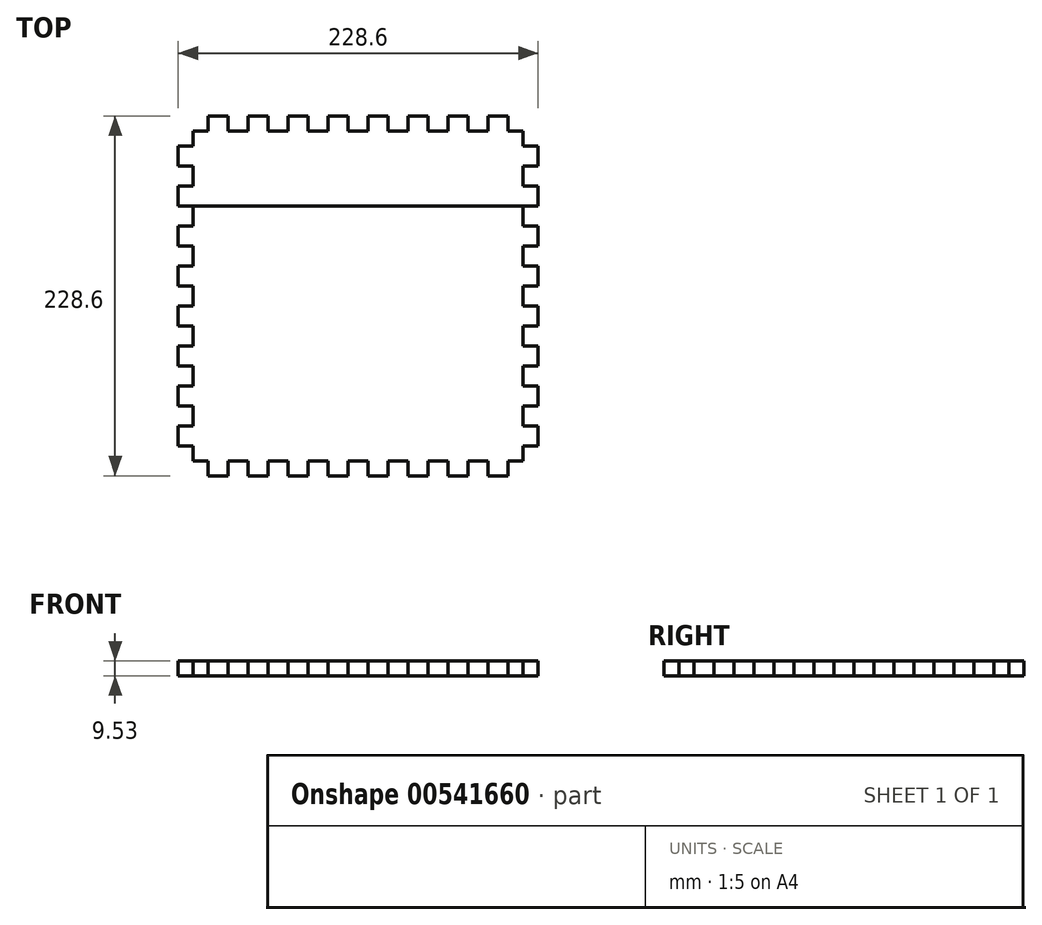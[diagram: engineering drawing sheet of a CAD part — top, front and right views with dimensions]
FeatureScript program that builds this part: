
annotation { "Feature Type Name" : "Feature", "Feature Type Description" : "" }
export const myFeature = defineFeature(function(context is Context, id is Id, definition is map)
    precondition{}
    {
        {
            var Q0;
            Q0=qCreatedBy(makeId("Top.planeOp"),FACE);
            var sketch = newSketch(context, id + "F0", { "sketchPlane" : qUnion([Q0])});
            skLineSegment(sketch, "E0.bottom", {"start": v(19.05, 0) * mm, "end": v(31.75, 0) * mm});
            skLineSegment(sketch, "E0.left", {"start": v(0, 0) * mm, "end": v(0, -31.75) * mm});
            skLineSegment(sketch, "E1", {"start": v(9.52, -9.52) * mm, "end": v(19.05, -9.52) * mm});
            skLineSegment(sketch, "E2", {"start": v(19.05, -9.53) * mm, "end": v(19.05, 0) * mm});
            skLineSegment(sketch, "E3", {"start": v(31.75, 0) * mm, "end": v(31.75, -9.53) * mm});
            skLineSegment(sketch, "E4", {"start": v(31.75, -9.53) * mm, "end": v(44.45, -9.53) * mm});
            skLineSegment(sketch, "E5", {"start": v(44.45, -9.53) * mm, "end": v(44.45, 0) * mm});
            skLineSegment(sketch, "E6", {"start": v(44.45, 0) * mm, "end": v(57.15, 0) * mm});
            skLineSegment(sketch, "E7", {"start": v(57.15, 0) * mm, "end": v(57.15, -9.53) * mm});
            skLineSegment(sketch, "E8", {"start": v(57.15, -9.53) * mm, "end": v(69.85, -9.53) * mm});
            skLineSegment(sketch, "E9", {"start": v(69.85, -9.53) * mm, "end": v(69.85, 0) * mm});
            skLineSegment(sketch, "E10", {"start": v(69.85, 0) * mm, "end": v(82.55, 0) * mm});
            skLineSegment(sketch, "E11", {"start": v(82.55, 0) * mm, "end": v(82.55, -9.53) * mm});
            skLineSegment(sketch, "E12", {"start": v(82.55, -9.53) * mm, "end": v(95.25, -9.53) * mm});
            skLineSegment(sketch, "E13", {"start": v(95.25, -9.53) * mm, "end": v(95.25, 0) * mm});
            skLineSegment(sketch, "E14.trimOffspring", {"start": v(95.25, 0) * mm, "end": v(107.95, 0) * mm});
            skLineSegment(sketch, "E15", {"start": v(107.95, 0) * mm, "end": v(107.95, -9.53) * mm});
            skLineSegment(sketch, "E16", {"start": v(107.95, -9.53) * mm, "end": v(120.65, -9.53) * mm});
            skLineSegment(sketch, "E17", {"start": v(120.65, -9.53) * mm, "end": v(120.65, 0) * mm});
            skLineSegment(sketch, "E18", {"start": v(120.65, 0) * mm, "end": v(133.35, 0) * mm});
            skLineSegment(sketch, "E19", {"start": v(133.35, 0) * mm, "end": v(133.35, -9.53) * mm});
            skLineSegment(sketch, "E20", {"start": v(133.35, -9.53) * mm, "end": v(146.05, -9.53) * mm});
            skLineSegment(sketch, "E21", {"start": v(146.05, -9.53) * mm, "end": v(146.05, 0) * mm});
            skLineSegment(sketch, "E22", {"start": v(146.05, 0) * mm, "end": v(158.75, 0) * mm});
            skLineSegment(sketch, "E23", {"start": v(158.75, 0) * mm, "end": v(158.75, -9.53) * mm});
            skLineSegment(sketch, "E24", {"start": v(158.75, -9.53) * mm, "end": v(171.45, -9.53) * mm});
            skLineSegment(sketch, "E25", {"start": v(171.45, -9.53) * mm, "end": v(171.45, 0) * mm});
            skLineSegment(sketch, "E26.trimOffspring", {"start": v(171.45, 0) * mm, "end": v(184.15, 0) * mm});
            skLineSegment(sketch, "E27", {"start": v(184.15, 0) * mm, "end": v(184.15, -9.52) * mm});
            skLineSegment(sketch, "E28", {"start": v(184.15, -9.52) * mm, "end": v(196.85, -9.52) * mm});
            skLineSegment(sketch, "E29", {"start": v(196.85, -9.52) * mm, "end": v(196.85, 0) * mm});
            skLineSegment(sketch, "E30", {"start": v(196.85, 0) * mm, "end": v(209.55, 0) * mm});
            skLineSegment(sketch, "E31", {"start": v(209.55, 0) * mm, "end": v(209.55, -9.52) * mm});
            skPoint(sketch, "E32.orphan", {"position": v(228.6, 0) * mm});
            skLineSegment(sketch, "E33", {"start": v(9.52, -9.53) * mm, "end": v(9.52, -19.05) * mm});
            skLineSegment(sketch, "E34", {"start": v(9.52, -19.05) * mm, "end": v(0, -19.05) * mm});
            skLineSegment(sketch, "E35", {"start": v(0, -19.05) * mm, "end": v(0, -31.75) * mm});
            skLineSegment(sketch, "E36", {"start": v(0, -31.75) * mm, "end": v(9.52, -31.75) * mm});
            skLineSegment(sketch, "E37", {"start": v(9.52, -31.75) * mm, "end": v(9.52, -44.45) * mm});
            skLineSegment(sketch, "E38", {"start": v(9.53, -44.45) * mm, "end": v(0, -44.45) * mm});
            skLineSegment(sketch, "E39", {"start": v(0, -44.45) * mm, "end": v(0, -57.15) * mm});
            skLineSegment(sketch, "E40", {"start": v(0, -57.15) * mm, "end": v(9.53, -57.15) * mm});
            skLineSegment(sketch, "E41", {"start": v(9.53, -57.15) * mm, "end": v(9.53, -69.85) * mm});
            skLineSegment(sketch, "E42", {"start": v(9.53, -69.85) * mm, "end": v(0, -69.85) * mm});
            skLineSegment(sketch, "E43", {"start": v(0, -69.85) * mm, "end": v(0, -82.55) * mm});
            skLineSegment(sketch, "E44", {"start": v(0, -82.55) * mm, "end": v(9.53, -82.55) * mm});
            skLineSegment(sketch, "E45", {"start": v(9.53, -82.55) * mm, "end": v(9.53, -95.25) * mm});
            skLineSegment(sketch, "E46", {"start": v(9.53, -95.25) * mm, "end": v(0, -95.25) * mm});
            skLineSegment(sketch, "E47.trimOffspring", {"start": v(0, -95.25) * mm, "end": v(0, -107.95) * mm});
            skLineSegment(sketch, "E48", {"start": v(0, -107.95) * mm, "end": v(9.53, -107.95) * mm});
            skLineSegment(sketch, "E49", {"start": v(9.53, -107.95) * mm, "end": v(9.53, -120.65) * mm});
            skLineSegment(sketch, "E50", {"start": v(9.53, -120.65) * mm, "end": v(0, -120.65) * mm});
            skLineSegment(sketch, "E51", {"start": v(0, -120.65) * mm, "end": v(0, -133.35) * mm});
            skLineSegment(sketch, "E52", {"start": v(0, -133.35) * mm, "end": v(9.53, -133.35) * mm});
            skLineSegment(sketch, "E53", {"start": v(9.53, -133.35) * mm, "end": v(9.53, -146.05) * mm});
            skLineSegment(sketch, "E54", {"start": v(9.53, -146.05) * mm, "end": v(0, -146.05) * mm});
            skLineSegment(sketch, "E55", {"start": v(0, -146.05) * mm, "end": v(0, -158.75) * mm});
            skLineSegment(sketch, "E56", {"start": v(0, -158.75) * mm, "end": v(9.53, -158.75) * mm});
            skLineSegment(sketch, "E57", {"start": v(9.53, -158.75) * mm, "end": v(9.53, -171.45) * mm});
            skLineSegment(sketch, "E58", {"start": v(9.53, -171.45) * mm, "end": v(0, -171.45) * mm});
            skLineSegment(sketch, "E59.trimOffspring", {"start": v(0, -171.45) * mm, "end": v(0, -184.15) * mm});
            skLineSegment(sketch, "E60", {"start": v(0, -184.15) * mm, "end": v(9.53, -184.15) * mm});
            skLineSegment(sketch, "E61", {"start": v(9.53, -184.15) * mm, "end": v(9.53, -196.85) * mm});
            skLineSegment(sketch, "E62", {"start": v(9.53, -196.85) * mm, "end": v(0, -196.85) * mm});
            skLineSegment(sketch, "E63", {"start": v(0, -196.85) * mm, "end": v(0, -209.55) * mm});
            skLineSegment(sketch, "E64", {"start": v(0, -209.55) * mm, "end": v(9.53, -209.55) * mm});
            skLineSegment(sketch, "E65", {"start": v(9.53, -209.55) * mm, "end": v(9.53, -219.07) * mm});
            skLineSegment(sketch, "E66", {"start": v(9.53, -219.07) * mm, "end": v(19.05, -219.07) * mm});
            skLineSegment(sketch, "E67", {"start": v(19.05, -219.07) * mm, "end": v(19.05, -228.6) * mm});
            skPoint(sketch, "E68.orphan", {"position": v(0, -228.6) * mm});
            skLineSegment(sketch, "E69", {"start": v(114.3, -9.53) * mm, "end": v(114.3, -55.4) * mm, "construction": true});
            skLineSegment(sketch, "E70", {"start": v(9.53, -114.3) * mm, "end": v(97.61, -114.3) * mm, "construction": true});
            skPoint(sketch, "E70.endSnap0", {"position": v(9.53, -114.3) * mm});
            skLineSegment(sketch, "E71.MirrorCS", {"start": v(219.08, -9.53) * mm, "end": v(219.08, -19.05) * mm});
            skLineSegment(sketch, "E72.MirrorCS", {"start": v(219.08, -19.05) * mm, "end": v(228.6, -19.05) * mm});
            skLineSegment(sketch, "E73.MirrorCS", {"start": v(228.6, -19.05) * mm, "end": v(228.6, -31.75) * mm});
            skLineSegment(sketch, "E74.MirrorCS", {"start": v(228.6, -31.75) * mm, "end": v(219.08, -31.75) * mm});
            skLineSegment(sketch, "E75.MirrorCS", {"start": v(219.08, -31.75) * mm, "end": v(219.08, -44.45) * mm});
            skLineSegment(sketch, "E76.MirrorCS", {"start": v(219.08, -44.45) * mm, "end": v(228.6, -44.45) * mm});
            skLineSegment(sketch, "E77.MirrorCS", {"start": v(228.6, -44.45) * mm, "end": v(228.6, -57.15) * mm});
            skLineSegment(sketch, "E78.MirrorCS", {"start": v(228.6, -57.15) * mm, "end": v(219.08, -57.15) * mm});
            skLineSegment(sketch, "E79.MirrorCS", {"start": v(219.08, -57.15) * mm, "end": v(219.08, -69.85) * mm});
            skLineSegment(sketch, "E80.MirrorCS", {"start": v(219.08, -69.85) * mm, "end": v(228.6, -69.85) * mm});
            skLineSegment(sketch, "E81.MirrorCS", {"start": v(228.6, -69.85) * mm, "end": v(228.6, -82.55) * mm});
            skLineSegment(sketch, "E82.MirrorCS", {"start": v(228.6, -82.55) * mm, "end": v(219.08, -82.55) * mm});
            skLineSegment(sketch, "E83.MirrorCS", {"start": v(219.08, -82.55) * mm, "end": v(219.08, -95.25) * mm});
            skLineSegment(sketch, "E84.MirrorCS", {"start": v(219.08, -95.25) * mm, "end": v(228.6, -95.25) * mm});
            skLineSegment(sketch, "E85.MirrorCS", {"start": v(228.6, -95.25) * mm, "end": v(228.6, -107.95) * mm});
            skLineSegment(sketch, "E86.MirrorCS", {"start": v(228.6, -107.95) * mm, "end": v(219.08, -107.95) * mm});
            skLineSegment(sketch, "E87.MirrorCS", {"start": v(219.08, -107.95) * mm, "end": v(219.08, -120.65) * mm});
            skLineSegment(sketch, "E88.MirrorCS", {"start": v(219.08, -120.65) * mm, "end": v(228.6, -120.65) * mm});
            skLineSegment(sketch, "E89.MirrorCS", {"start": v(228.6, -120.65) * mm, "end": v(228.6, -133.35) * mm});
            skLineSegment(sketch, "E90.MirrorCS", {"start": v(228.6, -133.35) * mm, "end": v(219.08, -133.35) * mm});
            skLineSegment(sketch, "E91.MirrorCS", {"start": v(219.08, -133.35) * mm, "end": v(219.08, -146.05) * mm});
            skLineSegment(sketch, "E92.MirrorCS", {"start": v(219.08, -146.05) * mm, "end": v(228.6, -146.05) * mm});
            skLineSegment(sketch, "E93.MirrorCS", {"start": v(228.6, -146.05) * mm, "end": v(228.6, -158.75) * mm});
            skLineSegment(sketch, "E94.MirrorCS", {"start": v(228.6, -158.75) * mm, "end": v(219.08, -158.75) * mm});
            skLineSegment(sketch, "E95.MirrorCS", {"start": v(219.08, -158.75) * mm, "end": v(219.08, -171.45) * mm});
            skLineSegment(sketch, "E96.MirrorCS", {"start": v(219.08, -171.45) * mm, "end": v(228.6, -171.45) * mm});
            skLineSegment(sketch, "E97.MirrorCS", {"start": v(228.6, -171.45) * mm, "end": v(228.6, -184.15) * mm});
            skLineSegment(sketch, "E98.MirrorCS", {"start": v(228.6, -184.15) * mm, "end": v(219.08, -184.15) * mm});
            skLineSegment(sketch, "E99.MirrorCS", {"start": v(219.08, -184.15) * mm, "end": v(219.08, -196.85) * mm});
            skLineSegment(sketch, "E100.MirrorCS", {"start": v(219.08, -196.85) * mm, "end": v(228.6, -196.85) * mm});
            skLineSegment(sketch, "E101.MirrorCS", {"start": v(228.6, -196.85) * mm, "end": v(228.6, -209.55) * mm});
            skLineSegment(sketch, "E102.MirrorCS", {"start": v(228.6, -209.55) * mm, "end": v(219.08, -209.55) * mm});
            skLineSegment(sketch, "E103.MirrorCS", {"start": v(219.08, -209.55) * mm, "end": v(219.08, -219.07) * mm});
            skLineSegment(sketch, "E104.MirrorCS", {"start": v(219.08, -219.07) * mm, "end": v(209.55, -219.07) * mm});
            skLineSegment(sketch, "E105.MirrorCS", {"start": v(209.55, -219.07) * mm, "end": v(209.55, -228.6) * mm});
            skLineSegment(sketch, "E106.MirrorCS", {"start": v(19.05, -228.6) * mm, "end": v(31.75, -228.6) * mm});
            skLineSegment(sketch, "E107.MirrorCS", {"start": v(31.75, -228.6) * mm, "end": v(31.75, -219.08) * mm});
            skLineSegment(sketch, "E108.MirrorCS", {"start": v(31.75, -219.08) * mm, "end": v(44.45, -219.08) * mm});
            skLineSegment(sketch, "E109.MirrorCS", {"start": v(44.45, -219.08) * mm, "end": v(44.45, -228.6) * mm});
            skLineSegment(sketch, "E110.MirrorCS", {"start": v(44.45, -228.6) * mm, "end": v(57.15, -228.6) * mm});
            skLineSegment(sketch, "E111.MirrorCS", {"start": v(57.15, -228.6) * mm, "end": v(57.15, -219.08) * mm});
            skLineSegment(sketch, "E112.MirrorCS", {"start": v(57.15, -219.08) * mm, "end": v(69.85, -219.08) * mm});
            skLineSegment(sketch, "E113.MirrorCS", {"start": v(69.85, -219.08) * mm, "end": v(69.85, -228.6) * mm});
            skLineSegment(sketch, "E114.MirrorCS", {"start": v(69.85, -228.6) * mm, "end": v(82.55, -228.6) * mm});
            skLineSegment(sketch, "E115.MirrorCS", {"start": v(82.55, -228.6) * mm, "end": v(82.55, -219.08) * mm});
            skLineSegment(sketch, "E116.MirrorCS", {"start": v(82.55, -219.08) * mm, "end": v(95.25, -219.08) * mm});
            skLineSegment(sketch, "E117.MirrorCS", {"start": v(95.25, -219.08) * mm, "end": v(95.25, -228.6) * mm});
            skLineSegment(sketch, "E118.MirrorCS", {"start": v(95.25, -228.6) * mm, "end": v(107.95, -228.6) * mm});
            skLineSegment(sketch, "E119.MirrorCS", {"start": v(107.95, -228.6) * mm, "end": v(107.95, -219.08) * mm});
            skLineSegment(sketch, "E120.MirrorCS", {"start": v(107.95, -219.08) * mm, "end": v(120.65, -219.08) * mm});
            skLineSegment(sketch, "E121.MirrorCS", {"start": v(120.65, -219.08) * mm, "end": v(120.65, -228.6) * mm});
            skLineSegment(sketch, "E122.MirrorCS", {"start": v(120.65, -228.6) * mm, "end": v(133.35, -228.6) * mm});
            skLineSegment(sketch, "E123.MirrorCS", {"start": v(133.35, -228.6) * mm, "end": v(133.35, -219.08) * mm});
            skLineSegment(sketch, "E124.MirrorCS", {"start": v(133.35, -219.08) * mm, "end": v(146.05, -219.08) * mm});
            skLineSegment(sketch, "E125.MirrorCS", {"start": v(146.05, -219.08) * mm, "end": v(146.05, -228.6) * mm});
            skLineSegment(sketch, "E126.MirrorCS", {"start": v(146.05, -228.6) * mm, "end": v(158.75, -228.6) * mm});
            skLineSegment(sketch, "E127.MirrorCS", {"start": v(158.75, -228.6) * mm, "end": v(158.75, -219.08) * mm});
            skLineSegment(sketch, "E128.MirrorCS", {"start": v(158.75, -219.08) * mm, "end": v(171.45, -219.08) * mm});
            skLineSegment(sketch, "E129.MirrorCS", {"start": v(171.45, -219.08) * mm, "end": v(171.45, -228.6) * mm});
            skLineSegment(sketch, "E130.MirrorCS", {"start": v(171.45, -228.6) * mm, "end": v(184.15, -228.6) * mm});
            skLineSegment(sketch, "E131.MirrorCS", {"start": v(184.15, -228.6) * mm, "end": v(184.15, -219.08) * mm});
            skLineSegment(sketch, "E132.MirrorCS", {"start": v(184.15, -219.08) * mm, "end": v(196.85, -219.08) * mm});
            skLineSegment(sketch, "E133.MirrorCS", {"start": v(196.85, -219.08) * mm, "end": v(196.85, -228.6) * mm});
            skLineSegment(sketch, "E134", {"start": v(196.85, -228.6) * mm, "end": v(209.55, -228.6) * mm});
            skLineSegment(sketch, "E135", {"start": v(209.55, -9.52) * mm, "end": v(219.08, -9.53) * mm});
            skLineSegment(sketch, "E136", {"start": v(9.53, -57.15) * mm, "end": v(219.08, -57.15) * mm});
            skSolve(sketch);
        }
        {
            var Q0;
            Q0=makeQuery(id+"F0.imprint","IMPRINT",FACE,{"disambiguationData":[TD([[makeQuery(id+"F0.imprint","IMPRINT",EDGE,{"derivedFrom":sQuery(id+"F0.wireOp",EDGE,"E0.bottom")}),-1.0]])]});
            extrude(context, id + "F1", {"entities" : qUnion([Q0]), "depth" : 9.52 * mm, "offsetDistance" : 25.4 * mm});
        }
        {
            var Q0;
            Q0=makeQuery(id+"F0.imprint","IMPRINT",FACE,{"disambiguationData":[TD([[makeQuery(id+"F0.imprint","IMPRINT",EDGE,{"derivedFrom":sQuery(id+"F0.wireOp",EDGE,"E41")}),1.0]])]});
            extrude(context, id + "F2", {"entities" : qUnion([Q0]), "depth" : 9.52 * mm, "offsetDistance" : 25.4 * mm});
        }
    });
